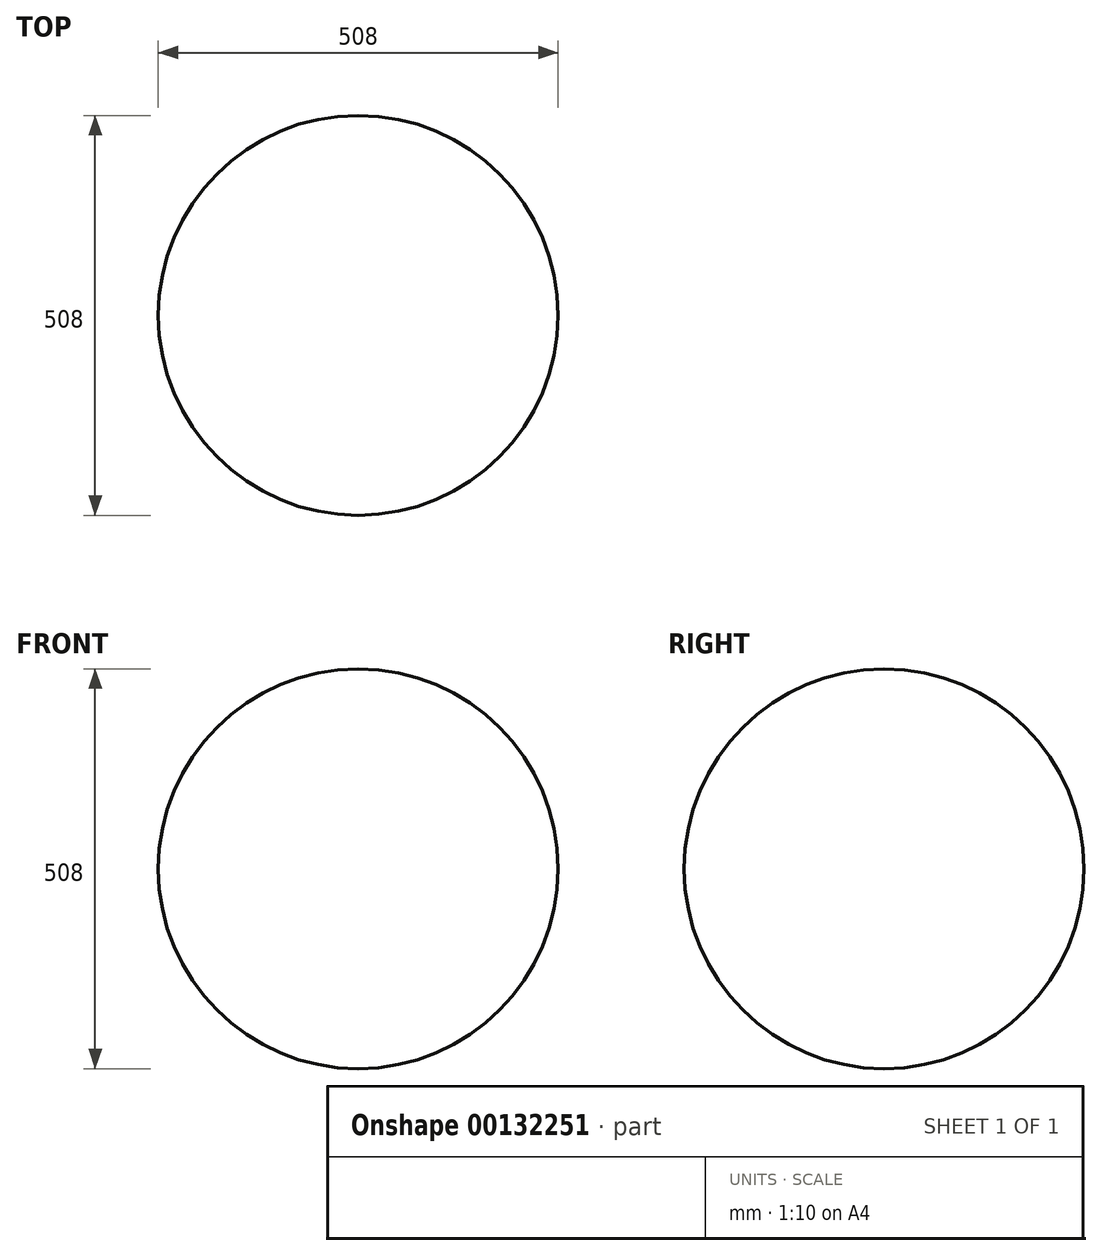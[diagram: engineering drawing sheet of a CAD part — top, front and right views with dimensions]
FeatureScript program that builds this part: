
annotation { "Feature Type Name" : "Feature", "Feature Type Description" : "" }
export const myFeature = defineFeature(function(context is Context, id is Id, definition is map)
    precondition{}
    {
        {
            var Q0;
            Q0=qCreatedBy(makeId("Front.planeOp"),FACE);
            var sketch = newSketch(context, id + "F0", { "sketchPlane" : qUnion([Q0])});
            skCircle(sketch, "E0", {"center": v(0, 0) * mm, "radius": 254 * mm});
            skLineSegment(sketch, "E1", {"start": v(-254, 0) * mm, "end": v(254, 0) * mm});
            skSolve(sketch);
        }
        {
            var Q0;
            {var subQ0=sQuery(id+"F0.wireOp",EDGE,"E1");Q0=makeQuery(id+"F0.imprint","IMPRINT",FACE,{"disambiguationData":[TD([[makeQuery(id+"F0.imprint","IMPRINT",EDGE,{"derivedFrom":subQ0}),-1.0]])]});}
            var Q1;
            Q1=sQuery(id+"F0.wireOp",EDGE,"E1");
            revolve(context, id + "F1", {"entities" : qUnion([Q0]), "axis" : qUnion([Q1]), "revolveType" : RevolveType.FULL});
        }
    });
